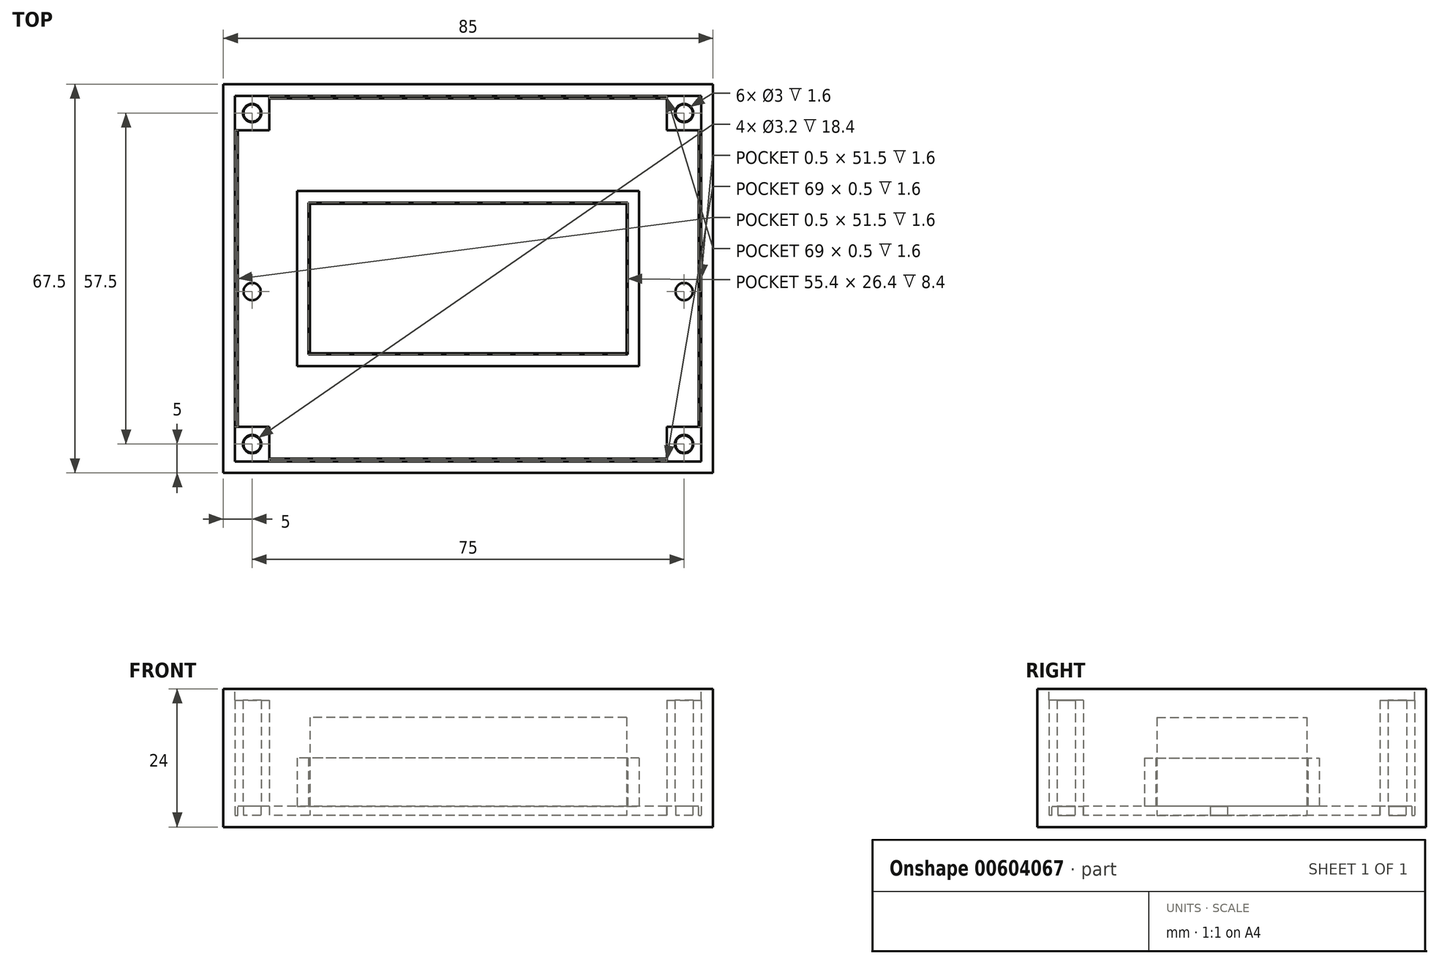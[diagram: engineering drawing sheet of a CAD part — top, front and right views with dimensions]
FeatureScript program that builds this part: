
annotation { "Feature Type Name" : "Feature", "Feature Type Description" : "" }
export const myFeature = defineFeature(function(context is Context, id is Id, definition is map)
    precondition{}
    {
        {
            assignVariable(context, id + "F0", {"name" : "Wall_thickness", "anyValue" : 2});
        }
        {
            var Q0;
            Q0=qCreatedBy(makeId("Top.planeOp"),FACE);
            var sketch = newSketch(context, id + "F1", { "sketchPlane" : qUnion([Q0])});
            skLineSegment(sketch, "E0.bottom", {"start": v(40, 31.25) * mm, "end": v(-40, 31.25) * mm});
            skLineSegment(sketch, "E0.top", {"start": v(40, -31.25) * mm, "end": v(-40, -31.25) * mm});
            skLineSegment(sketch, "E0.left", {"start": v(40, 31.25) * mm, "end": v(40, -31.25) * mm});
            skLineSegment(sketch, "E0.right", {"start": v(-40, 31.25) * mm, "end": v(-40, -31.25) * mm});
            skPoint(sketch, "E0.middle", {"position": v(0, 0) * mm});
            skCircle(sketch, "E1", {"center": v(-37.5, -28.75) * mm, "radius": 1.5 * mm});
            skCircle(sketch, "E2", {"center": v(-37.5, 28.75) * mm, "radius": 1.5 * mm});
            skCircle(sketch, "E3", {"center": v(37.5, 28.75) * mm, "radius": 1.5 * mm});
            skCircle(sketch, "E4", {"center": v(37.5, -28.75) * mm, "radius": 1.5 * mm});
            skLineSegment(sketch, "E5.bottom", {"start": v(37.5, 28.75) * mm, "end": v(-37.5, 28.75) * mm, "construction": true});
            skLineSegment(sketch, "E5.top", {"start": v(37.5, -28.75) * mm, "end": v(-37.5, -28.75) * mm, "construction": true});
            skLineSegment(sketch, "E5.left", {"start": v(37.5, 28.75) * mm, "end": v(37.5, -28.75) * mm, "construction": true});
            skLineSegment(sketch, "E5.right", {"start": v(-37.5, 28.75) * mm, "end": v(-37.5, -28.75) * mm, "construction": true});
            skCircle(sketch, "E6", {"center": v(-37.5, -2.25) * mm, "radius": 1.5 * mm});
            skCircle(sketch, "E7", {"center": v(37.5, -2.25) * mm, "radius": 1.5 * mm});
            skSolve(sketch);
        }
        {
            var Q0;
            Q0 = qSketchRegion(id + "F1", true);
            extrude(context, id + "F2", {"entities" : qUnion([Q0]), "depth" : 1.6 * mm, "offsetDistance" : 25 * mm});
        }
        {
            var Q0;
            Q0=qCreatedBy(makeId("Top.planeOp"),FACE);
            var sketch = newSketch(context, id + "F3", { "sketchPlane" : qUnion([Q0])});
            skLineSegment(sketch, "E8.bottom", {"start": v(40.5, 31.75) * mm, "end": v(-40.5, 31.75) * mm});
            skLineSegment(sketch, "E8.top", {"start": v(40.5, -31.75) * mm, "end": v(-40.5, -31.75) * mm});
            skLineSegment(sketch, "E8.left", {"start": v(40.5, 31.75) * mm, "end": v(40.5, -31.75) * mm});
            skLineSegment(sketch, "E8.right", {"start": v(-40.5, 31.75) * mm, "end": v(-40.5, -31.75) * mm});
            skPoint(sketch, "E8.middle", {"position": v(0, 0) * mm});
            skLineSegment(sketch, "E9.0", {"start": v(-42.5, 33.75) * mm, "end": v(-42.5, -33.75) * mm});
            skLineSegment(sketch, "E9.1", {"start": v(42.5, 33.75) * mm, "end": v(-42.5, 33.75) * mm});
            skLineSegment(sketch, "E9.2", {"start": v(42.5, 33.75) * mm, "end": v(42.5, -33.75) * mm});
            skLineSegment(sketch, "E9.3", {"start": v(42.5, -33.75) * mm, "end": v(-42.5, -33.75) * mm});
            skPoint(sketch, "E10.middle", {"position": v(-37.5, -28.75) * mm});
            skPoint(sketch, "E11.middle", {"position": v(-37.5, 28.75) * mm});
            skPoint(sketch, "E12.middle", {"position": v(37.5, 28.75) * mm});
            skPoint(sketch, "E13.middle", {"position": v(37.5, -28.75) * mm});
            skCircle(sketch, "E14", {"center": v(-37.5, 28.75) * mm, "radius": 1.6 * mm});
            skCircle(sketch, "E15", {"center": v(37.5, 28.75) * mm, "radius": 1.6 * mm});
            skCircle(sketch, "E16", {"center": v(37.5, -28.75) * mm, "radius": 1.6 * mm});
            skCircle(sketch, "E17", {"center": v(-37.5, -28.75) * mm, "radius": 1.6 * mm});
            skLineSegment(sketch, "E18", {"start": v(-40.5, 25.75) * mm, "end": v(-34.5, 25.75) * mm});
            skLineSegment(sketch, "E19", {"start": v(-34.5, 25.75) * mm, "end": v(-34.5, 31.75) * mm});
            skLineSegment(sketch, "E20", {"start": v(-37.5, 25.75) * mm, "end": v(-37.5, 31.75) * mm, "construction": true});
            skLineSegment(sketch, "E21", {"start": v(-40.5, -25.75) * mm, "end": v(-34.5, -25.75) * mm});
            skLineSegment(sketch, "E22", {"start": v(-34.5, -25.75) * mm, "end": v(-34.5, -31.75) * mm});
            skLineSegment(sketch, "E23", {"start": v(-37.5, -25.75) * mm, "end": v(-37.5, -31.75) * mm, "construction": true});
            skLineSegment(sketch, "E24", {"start": v(34.5, -25.75) * mm, "end": v(40.5, -25.75) * mm});
            skLineSegment(sketch, "E25", {"start": v(34.5, -25.75) * mm, "end": v(34.5, -31.75) * mm});
            skLineSegment(sketch, "E26", {"start": v(37.5, -25.75) * mm, "end": v(37.5, -31.75) * mm, "construction": true});
            skLineSegment(sketch, "E27", {"start": v(34.5, 31.75) * mm, "end": v(34.5, 25.75) * mm});
            skLineSegment(sketch, "E28", {"start": v(34.5, 25.75) * mm, "end": v(40.5, 25.75) * mm});
            skLineSegment(sketch, "E29", {"start": v(37.5, 25.75) * mm, "end": v(37.5, 31.75) * mm, "construction": true});
            skSolve(sketch);
        }
        {
            var Q0;
            Q0=makeQuery(id+"F3.imprint","IMPRINT",FACE,{"disambiguationData":[TD([[makeQuery(id+"F3.imprint","IMPRINT",EDGE,{"derivedFrom":sQuery(id+"F3.wireOp",EDGE,"E9.0")}),1.0]])]});
            var Q1;
            Q1=makeQuery(id+"F3.imprint","IMPRINT",FACE,{"disambiguationData":[TD([[makeQuery(id+"F3.imprint","IMPRINT",EDGE,{"derivedFrom":sQuery(id+"F3.wireOp",EDGE,"E14")}),-1.0]])]});
            var Q2;
            Q2=makeQuery(id+"F3.imprint","IMPRINT",FACE,{"disambiguationData":[TD([[makeQuery(id+"F3.imprint","IMPRINT",EDGE,{"derivedFrom":sQuery(id+"F3.wireOp",EDGE,"E14")}),1.0]])]});
            var Q3;
            {var subQ6=sQuery(id+"F3.wireOp",EDGE,"E18");Q3=makeQuery(id+"F3.imprint","IMPRINT",FACE,{"disambiguationData":[TD([[makeQuery(id+"F3.imprint","IMPRINT",EDGE,{"derivedFrom":subQ6}),-1.0]])]});}
            var Q4;
            Q4=makeQuery(id+"F3.imprint","IMPRINT",FACE,{"disambiguationData":[TD([[makeQuery(id+"F3.imprint","IMPRINT",EDGE,{"derivedFrom":sQuery(id+"F3.wireOp",EDGE,"E15")}),-1.0]])]});
            var Q5;
            Q5=makeQuery(id+"F3.imprint","IMPRINT",FACE,{"disambiguationData":[TD([[makeQuery(id+"F3.imprint","IMPRINT",EDGE,{"derivedFrom":sQuery(id+"F3.wireOp",EDGE,"E15")}),1.0]])]});
            var Q6;
            Q6=makeQuery(id+"F3.imprint","IMPRINT",FACE,{"disambiguationData":[TD([[makeQuery(id+"F3.imprint","IMPRINT",EDGE,{"derivedFrom":sQuery(id+"F3.wireOp",EDGE,"E16")}),-1.0]])]});
            var Q7;
            Q7=makeQuery(id+"F3.imprint","IMPRINT",FACE,{"disambiguationData":[TD([[makeQuery(id+"F3.imprint","IMPRINT",EDGE,{"derivedFrom":sQuery(id+"F3.wireOp",EDGE,"E16")}),1.0]])]});
            var Q8;
            Q8=makeQuery(id+"F3.imprint","IMPRINT",FACE,{"disambiguationData":[TD([[makeQuery(id+"F3.imprint","IMPRINT",EDGE,{"derivedFrom":sQuery(id+"F3.wireOp",EDGE,"E17")}),-1.0]])]});
            var Q9;
            Q9=makeQuery(id+"F3.imprint","IMPRINT",FACE,{"disambiguationData":[TD([[makeQuery(id+"F3.imprint","IMPRINT",EDGE,{"derivedFrom":sQuery(id+"F3.wireOp",EDGE,"E17")}),1.0]])]});
            extrude(context, id + "F4", {"entities" : qUnion([Q0, Q1, Q2, Q3, Q4, Q5, Q6, Q7, Q8, Q9]), "depth" : (-getVariable(context, 'Wall_thickness')) * mm, "offsetDistance" : 25 * mm});
        }
        {
            var Q0;
            Q0=makeQuery(id+"F3.imprint","IMPRINT",FACE,{"disambiguationData":[TD([[makeQuery(id+"F3.imprint","IMPRINT",EDGE,{"derivedFrom":sQuery(id+"F3.wireOp",EDGE,"E14")}),-1.0]])]});
            var Q1;
            Q1=makeQuery(id+"F3.imprint","IMPRINT",FACE,{"disambiguationData":[TD([[makeQuery(id+"F3.imprint","IMPRINT",EDGE,{"derivedFrom":sQuery(id+"F3.wireOp",EDGE,"E9.0")}),1.0]])]});
            var Q2;
            Q2=makeQuery(id+"F3.imprint","IMPRINT",FACE,{"disambiguationData":[TD([[makeQuery(id+"F3.imprint","IMPRINT",EDGE,{"derivedFrom":sQuery(id+"F3.wireOp",EDGE,"E15")}),-1.0]])]});
            var Q3;
            Q3=makeQuery(id+"F3.imprint","IMPRINT",FACE,{"disambiguationData":[TD([[makeQuery(id+"F3.imprint","IMPRINT",EDGE,{"derivedFrom":sQuery(id+"F3.wireOp",EDGE,"E16")}),-1.0]])]});
            var Q4;
            Q4=makeQuery(id+"F3.imprint","IMPRINT",FACE,{"disambiguationData":[TD([[makeQuery(id+"F3.imprint","IMPRINT",EDGE,{"derivedFrom":sQuery(id+"F3.wireOp",EDGE,"E17")}),-1.0]])]});
            extrude(context, id + "F5", {"entities" : qUnion([Q0, Q1, Q2, Q3, Q4]), "operationType" : NewBodyOperationType.ADD, "depth" : 22 * mm, "offsetDistance" : 25 * mm});
        }
        {
            var Q0;
            Q0=makeQuery(id+"F5.opExtrude","CAP_FACE",FACE,{"disambiguationData":[OSD([sQuery(id+"F3.wireOp",EDGE,"E8.bottom"),sQuery(id+"F3.wireOp",EDGE,"E8.top"),sQuery(id+"F3.wireOp",EDGE,"E8.left"),sQuery(id+"F3.wireOp",EDGE,"E8.right"),sQuery(id+"F3.wireOp",EDGE,"E9.0"),sQuery(id+"F3.wireOp",EDGE,"E9.1"),sQuery(id+"F3.wireOp",EDGE,"E9.2"),sQuery(id+"F3.wireOp",EDGE,"E9.3"),sQuery(id+"F3.wireOp",EDGE,"E11.bottom"),sQuery(id+"F3.wireOp",EDGE,"E11.left"),sQuery(id+"F3.wireOp",EDGE,"E12.bottom"),sQuery(id+"F3.wireOp",EDGE,"E12.left"),sQuery(id+"F3.wireOp",EDGE,"E13.bottom"),sQuery(id+"F3.wireOp",EDGE,"E13.left"),sQuery(id+"F3.wireOp",EDGE,"521CgIRV-P5lj-AM5o-2Uwu-cH4HPtEPasYc.top"),sQuery(id+"F3.wireOp",EDGE,"521CgIRV-P5lj-AM5o-2Uwu-cH4HPtEPasYc.left"),sQuery(id+"F3.wireOp",EDGE,"E14"),sQuery(id+"F3.wireOp",EDGE,"E15"),sQuery(id+"F3.wireOp",EDGE,"E16"),sQuery(id+"F3.wireOp",EDGE,"E17")])],"isStart":false});
            var sketch = newSketch(context, id + "F6", { "sketchPlane" : qUnion([Q0])});
            skLineSegment(sketch, "E30.0", {"start": v(-40.5, 31.75) * mm, "end": v(-40.5, -31.75) * mm});
            skLineSegment(sketch, "E31.0", {"start": v(40.5, 31.75) * mm, "end": v(-40.5, 31.75) * mm});
            skLineSegment(sketch, "E32.0", {"start": v(-34.5, 25.75) * mm, "end": v(-34.5, 31.75) * mm});
            skLineSegment(sketch, "E33.0", {"start": v(-40.5, 25.75) * mm, "end": v(-34.5, 25.75) * mm});
            skCircle(sketch, "E34.0", {"center": v(-37.5, 28.75) * mm, "radius": 1.6 * mm});
            skLineSegment(sketch, "E35.0", {"start": v(-40.5, -25.75) * mm, "end": v(-34.5, -25.75) * mm});
            skLineSegment(sketch, "E36.0", {"start": v(-34.5, -25.75) * mm, "end": v(-34.5, -31.75) * mm});
            skLineSegment(sketch, "E37.0", {"start": v(40.5, -31.75) * mm, "end": v(-40.5, -31.75) * mm});
            skCircle(sketch, "E38.0", {"center": v(-37.5, -28.75) * mm, "radius": 1.6 * mm});
            skLineSegment(sketch, "E39.0", {"start": v(34.5, -25.75) * mm, "end": v(40.5, -25.75) * mm});
            skLineSegment(sketch, "E40.0", {"start": v(34.5, -25.75) * mm, "end": v(34.5, -31.75) * mm});
            skCircle(sketch, "E41.0", {"center": v(37.5, -28.75) * mm, "radius": 1.6 * mm});
            skLineSegment(sketch, "E42.0", {"start": v(40.5, 31.75) * mm, "end": v(40.5, -31.75) * mm});
            skCircle(sketch, "E43.0", {"center": v(37.5, 28.75) * mm, "radius": 1.6 * mm});
            skLineSegment(sketch, "E44.0", {"start": v(34.5, 31.75) * mm, "end": v(34.5, 25.75) * mm});
            skLineSegment(sketch, "E45.0", {"start": v(34.5, 25.75) * mm, "end": v(40.5, 25.75) * mm});
            skSolve(sketch);
        }
        {
            var Q0;
            {var subQ1=sQuery(id+"F6.wireOp",EDGE,"E32.0");Q0=makeQuery(id+"F6.imprint","IMPRINT",FACE,{"disambiguationData":[TD([[makeQuery(id+"F6.imprint","IMPRINT",EDGE,{"derivedFrom":subQ1}),1.0]])]});}
            var Q1;
            {var subQ4=sQuery(id+"F6.wireOp",EDGE,"E35.0");Q1=makeQuery(id+"F6.imprint","IMPRINT",FACE,{"disambiguationData":[TD([[makeQuery(id+"F6.imprint","IMPRINT",EDGE,{"derivedFrom":subQ4}),-1.0]])]});}
            var Q2;
            Q2=makeQuery(id+"F6.imprint","IMPRINT",FACE,{"disambiguationData":[TD([[makeQuery(id+"F6.imprint","IMPRINT",EDGE,{"derivedFrom":sQuery(id+"F6.wireOp",EDGE,"E43.0")}),-1.0]])]});
            var Q3;
            {var subQ0=sQuery(id+"F6.wireOp",EDGE,"E39.0");Q3=makeQuery(id+"F6.imprint","IMPRINT",FACE,{"disambiguationData":[TD([[makeQuery(id+"F6.imprint","IMPRINT",EDGE,{"derivedFrom":subQ0}),-1.0]])]});}
            extrude(context, id + "F7", {"entities" : qUnion([Q0, Q1, Q2, Q3]), "operationType" : NewBodyOperationType.REMOVE, "oppositeDirection" : true, "depth" : 2 * mm, "offsetDistance" : 25 * mm});
        }
        {
            var Q0;
            Q0=qCreatedBy(makeId("Top.planeOp"),FACE);
            var sketch = newSketch(context, id + "F8", { "sketchPlane" : qUnion([Q0])});
            skLineSegment(sketch, "E46.bottom", {"start": v(27.5, -13) * mm, "end": v(-27.5, -13) * mm});
            skLineSegment(sketch, "E46.top", {"start": v(27.5, 13) * mm, "end": v(-27.5, 13) * mm});
            skLineSegment(sketch, "E46.left", {"start": v(27.5, -13) * mm, "end": v(27.5, 13) * mm});
            skLineSegment(sketch, "E46.right", {"start": v(-27.5, -13) * mm, "end": v(-27.5, 13) * mm});
            skPoint(sketch, "E46.middle", {"position": v(0, 0) * mm});
            skSolve(sketch);
        }
        {
            var Q0;
            Q0=makeQuery(id+"F8.imprint","IMPRINT",FACE,{"disambiguationData":[TD([[makeQuery(id+"F8.imprint","IMPRINT",EDGE,{"derivedFrom":sQuery(id+"F8.wireOp",EDGE,"E46.bottom")}),-1.0]])]});
            extrude(context, id + "F9", {"entities" : qUnion([Q0]), "depth" : 17 * mm, "offsetDistance" : 25 * mm});
        }
        {
            var Q0;
            Q0=makeQuery(id+"F5.boolean.opBoolean","SPLIT",FACE,{"disambiguationData":[TD([makeQuery(id+"F5.opExtrude","SWEPT_FACE",FACE,{"disambiguationData":[OSD([sQuery(id+"F3.wireOp",EDGE,"E8.bottom")])]})])],"derivedFrom":makeQuery(id+"F4.opExtrude","CAP_FACE",FACE,{"disambiguationData":[OSD([sQuery(id+"F3.wireOp",EDGE,"E9.0"),sQuery(id+"F3.wireOp",EDGE,"E9.1"),sQuery(id+"F3.wireOp",EDGE,"E9.2"),sQuery(id+"F3.wireOp",EDGE,"E9.3")])],"isStart":true})});
            var sketch = newSketch(context, id + "F10", { "sketchPlane" : qUnion([Q0])});
            skLineSegment(sketch, "E47.0", {"start": v(27.7, 13.2) * mm, "end": v(-27.7, 13.2) * mm});
            skLineSegment(sketch, "E47.1", {"start": v(27.7, -13.2) * mm, "end": v(27.7, 13.2) * mm});
            skLineSegment(sketch, "E47.2", {"start": v(27.7, -13.2) * mm, "end": v(-27.7, -13.2) * mm});
            skLineSegment(sketch, "E47.3", {"start": v(-27.7, -13.2) * mm, "end": v(-27.7, 13.2) * mm});
            skLineSegment(sketch, "E48.0", {"start": v(29.7, 15.2) * mm, "end": v(-29.7, 15.2) * mm});
            skLineSegment(sketch, "E48.1", {"start": v(29.7, -15.2) * mm, "end": v(29.7, 15.2) * mm});
            skLineSegment(sketch, "E48.2", {"start": v(29.7, -15.2) * mm, "end": v(-29.7, -15.2) * mm});
            skLineSegment(sketch, "E48.3", {"start": v(-29.7, -15.2) * mm, "end": v(-29.7, 15.2) * mm});
            skSolve(sketch);
        }
        {
            var Q0;
            Q0=makeQuery(id+"F10.imprint","IMPRINT",FACE,{"disambiguationData":[TD([[makeQuery(id+"F10.imprint","IMPRINT",EDGE,{"derivedFrom":sQuery(id+"F10.wireOp",EDGE,"E47.0")}),-1.0]])]});
            extrude(context, id + "F11", {"entities" : qUnion([Q0]), "operationType" : NewBodyOperationType.ADD, "depth" : 10 * mm, "offsetDistance" : 25 * mm});
        }
    });
